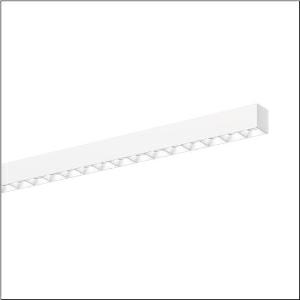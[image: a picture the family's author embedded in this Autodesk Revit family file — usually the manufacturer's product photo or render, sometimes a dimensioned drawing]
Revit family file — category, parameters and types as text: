
# Revit family: silica_r__21_51mx26db35wb_1250
name_source: partatom
category: Lighting Fixtures
units: mm (PartAtom-declared; Revit-internal decimal feet)

## family parameters
Cut with Voids When Loaded = No
Host = Face
Light Source = No
Part Type = Normal
Room Calculation Point = No
Round Connector Dimension = Use Diameter
Shared = No

## types (1)
- --- (1 x LED, 5400 lm, 31.4 W, 3000K)
    Apparent Load = 31 VA
    CIE Flux Codes = 83 98 100 100 100
    Color Rendering = 80
    Color Temperature = 3000K
    Default Elevation = 1800 mm
    Description = Silica® 21, office luminaire, primary light control with darklight reflector, of PMMA, white, CAT 2 (L<= 3000cd/m²), light emission: direct distribution, primary light characteristic: symmetric, installation type: surface-mounted, LED, rated luminous flux: 5.400lm, luminous efficacy: 172lm/W, light colour: 830, colour temperature: 3000K, with terminal, 3+2-pole, max. 2.5mm², mains connection: 220..240V, AC, 50/60Hz, rated input power: 31.4W, luminaire housing, of aluminium, traffic white (RAL 9016), length: 1.504mm, width: 53mm, height: 53mm, protection rating (complete): IP20, insulation class (complete): insulation class I (protective earthing), certification: CE, permissible operating ambient temperature: 0..+35°C, standard: EN 50419, packaging unit: 1 piece
    Height = 0 mm  [stored 0 ft]
    Lamp = 1 x LED
    Lamp Light Flux = 5400 lm
    Lamp Power = 31.4 W
    Lamp count = 1
    Length = 1504 mm
    Luminous efficacy = 172 lm/W
    Manufacturer = Siteco
    ModVariant = No
    Model = 51MX26DB35WB
    Mounting Place = Ceiling
    Mounting Type = Recessed
    Number of Poles = 1
    OnlyDefault = Yes
    Power Factor = 1
    Product Name = Silica® 21
    Product group = office luminaire | ceiling recessed
    ProductGroupID = 400
    Protection Class = Protection class I
    Protection Degree = IP 20
    RLX_Detail_Level = 1
    RLX_Emergency_Light_Flux = 0 lm
    RLX_Emergency_Type = 0
    RLX_Emergency_Type_DB = No
    RlxData = <blob elided: 41765 chars, md5=1eb9669b>
    Socket = socket
    Standby Power = 0 W
    System Light Flux = 5400 lm
    System Power = 31 W
    Type Comments = factory setting: luminous flux: 100 % | dim-lin: 254 | 360 mA
    Type Image = l_1335934.jpg
    URL = http://relux.com
    VarID = @adj_094175
    Voltage = 0 V
    Weight = 0.00 kg
    Width = 53 mm

note: [stored X ft] marks values corroborated as IEEE doubles in the binary element streams (Revit-internal decimal feet)

## geometry (parser evidence)
native form markers: Blend x4, Sweep x11
no freeform markers — native parametric forms only
